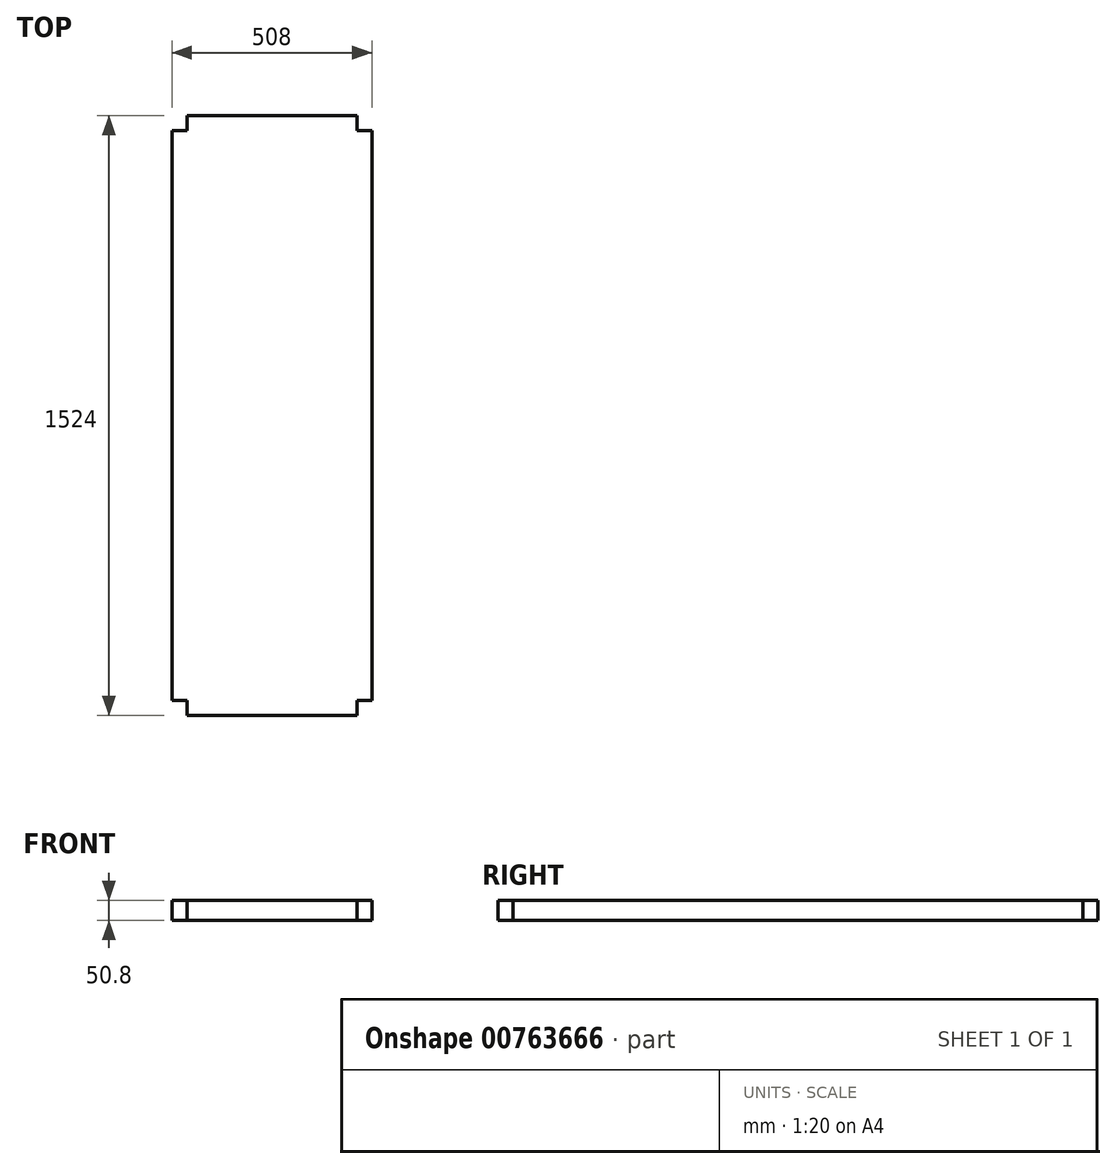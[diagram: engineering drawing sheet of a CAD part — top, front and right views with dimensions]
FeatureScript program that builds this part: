
annotation { "Feature Type Name" : "Feature", "Feature Type Description" : "" }
export const myFeature = defineFeature(function(context is Context, id is Id, definition is map)
    precondition{}
    {
        {
            var Q0;
            Q0=qCreatedBy(makeId("Top.planeOp"),FACE);
            var sketch = newSketch(context, id + "F0", { "sketchPlane" : qUnion([Q0])});
            skLineSegment(sketch, "E0.bottom", {"start": v(-244.65, -589.1) * mm, "end": v(187.15, -589.1) * mm});
            skLineSegment(sketch, "E0.top", {"start": v(-244.65, 934.9) * mm, "end": v(187.15, 934.9) * mm});
            skLineSegment(sketch, "E0.left", {"start": v(-282.75, -551) * mm, "end": v(-282.75, 896.8) * mm});
            skLineSegment(sketch, "E0.right", {"start": v(225.25, -551) * mm, "end": v(225.25, 896.8) * mm});
            skPoint(sketch, "E0.middle", {"position": v(-28.75, 172.9) * mm});
            skLineSegment(sketch, "E1.top", {"start": v(-282.75, 896.8) * mm, "end": v(-244.65, 896.8) * mm});
            skLineSegment(sketch, "E1.right", {"start": v(-244.65, 934.9) * mm, "end": v(-244.65, 896.8) * mm});
            skLineSegment(sketch, "E2.top", {"start": v(225.25, 896.8) * mm, "end": v(187.15, 896.8) * mm});
            skLineSegment(sketch, "E2.right", {"start": v(187.15, 934.9) * mm, "end": v(187.15, 896.8) * mm});
            skLineSegment(sketch, "E3.top", {"start": v(225.25, -551) * mm, "end": v(187.15, -551) * mm});
            skLineSegment(sketch, "E3.right", {"start": v(187.15, -589.1) * mm, "end": v(187.15, -551) * mm});
            skLineSegment(sketch, "E4.top", {"start": v(-282.75, -551) * mm, "end": v(-244.65, -551) * mm});
            skLineSegment(sketch, "E4.right", {"start": v(-244.65, -589.1) * mm, "end": v(-244.65, -551) * mm});
            skPoint(sketch, "E4.left.start.orphan", {"position": v(-282.75, -589.1) * mm});
            skPoint(sketch, "E5.orphan", {"position": v(225.25, -589.1) * mm});
            skPoint(sketch, "E6.orphan", {"position": v(225.25, 934.9) * mm});
            skPoint(sketch, "E7.orphan", {"position": v(-282.75, 934.9) * mm});
            skSolve(sketch);
        }
        {
            var Q0;
            Q0=makeQuery(id+"F0.imprint","IMPRINT",FACE,{"disambiguationData":[TD([[makeQuery(id+"F0.imprint","IMPRINT",EDGE,{"derivedFrom":sQuery(id+"F0.wireOp",EDGE,"E0.bottom")}),1.0]])]});
            extrude(context, id + "F1", {"entities" : qUnion([Q0]), "oppositeDirection" : true, "depth" : 50.8 * mm, "offsetDistance" : 25.4 * mm});
        }
    });
